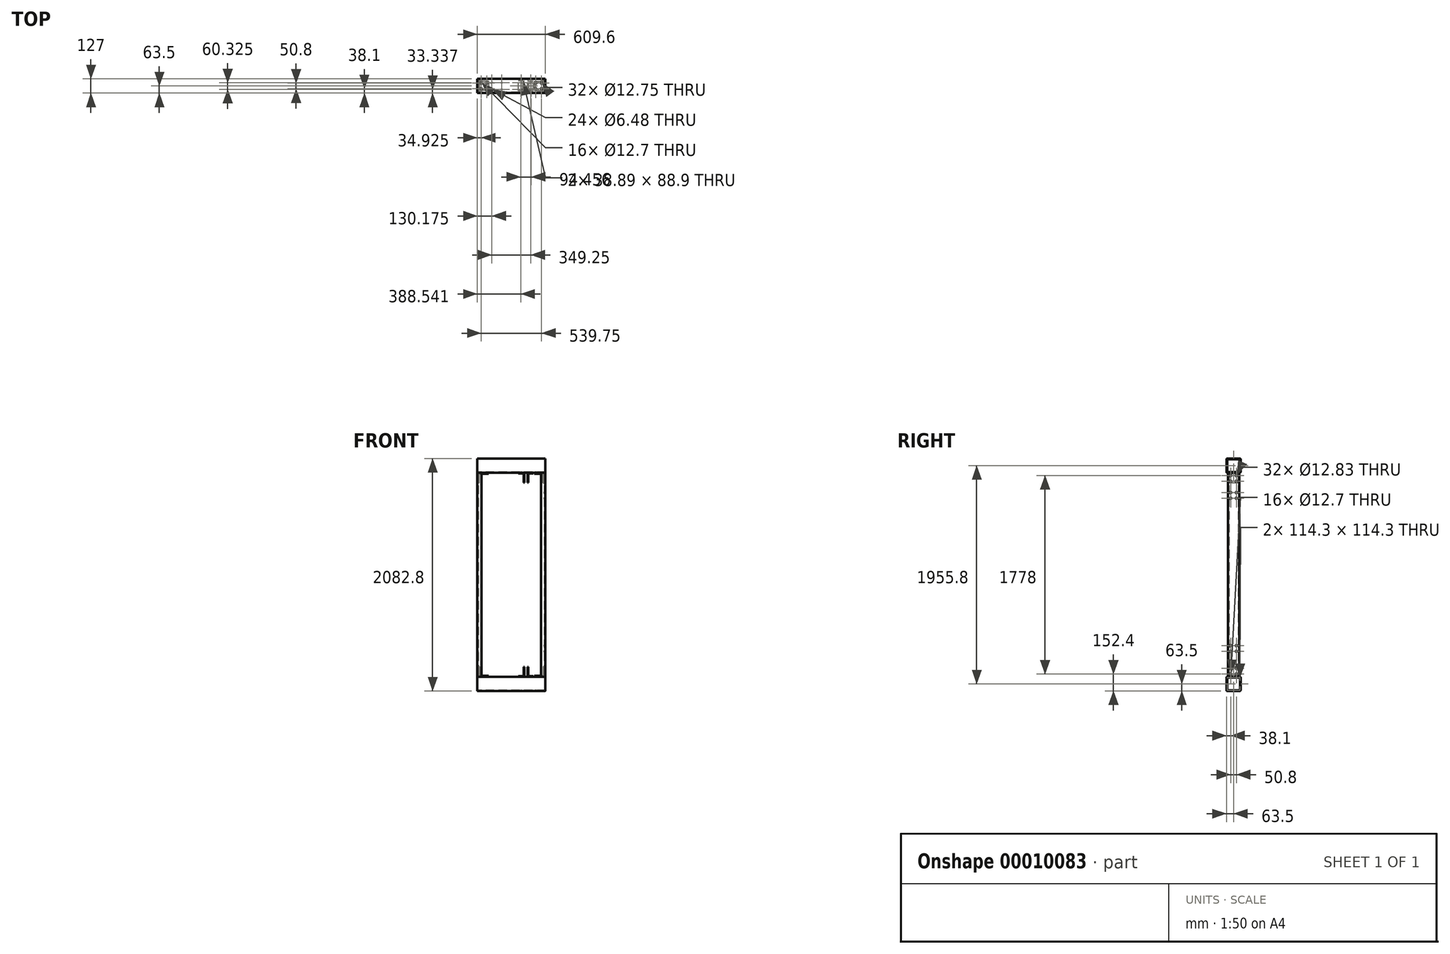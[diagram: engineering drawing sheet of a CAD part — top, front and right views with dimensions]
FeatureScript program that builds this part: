
annotation { "Feature Type Name" : "Feature", "Feature Type Description" : "" }
export const myFeature = defineFeature(function(context is Context, id is Id, definition is map)
    precondition{}
    {
        {
            var Q0;
            Q0=qCreatedBy(makeId("Front.planeOp"),FACE);
            cPlane(context, id + "F0", {"entities" : qUnion([Q0]), "cplaneType" : CPlaneType.OFFSET, "offset" : 41.27 * mm, "width" : 152.4 * mm, "height" : 152.4 * mm});
        }
        {
            var Q0;
            Q0=qCreatedBy(makeId("Top.planeOp"),FACE);
            cPlane(context, id + "F1", {"entities" : qUnion([Q0]), "cplaneType" : CPlaneType.OFFSET, "offset" : 977.9 * mm, "width" : 152.4 * mm, "height" : 152.4 * mm});
        }
        {
            var Q0;
            Q0=qCreatedBy(makeId("Right.planeOp"),FACE);
            var sketch = newSketch(context, id + "F2", { "sketchPlane" : qUnion([Q0])});
            skLineSegment(sketch, "E0.bottom", {"start": v(-57.15, 63.5) * mm, "end": v(57.15, 63.5) * mm});
            skLineSegment(sketch, "E0.top", {"start": v(-57.15, -63.5) * mm, "end": v(57.15, -63.5) * mm});
            skLineSegment(sketch, "E0.left", {"start": v(-63.5, 57.15) * mm, "end": v(-63.5, -57.15) * mm});
            skLineSegment(sketch, "E0.right", {"start": v(63.5, 57.15) * mm, "end": v(63.5, -57.15) * mm});
            skLineSegment(sketch, "E1.bottom", {"start": v(-57.15, 57.15) * mm, "end": v(57.15, 57.15) * mm});
            skLineSegment(sketch, "E1.top", {"start": v(-57.15, -57.15) * mm, "end": v(57.15, -57.15) * mm});
            skLineSegment(sketch, "E1.left", {"start": v(-57.15, 57.15) * mm, "end": v(-57.15, -57.15) * mm});
            skLineSegment(sketch, "E1.right", {"start": v(57.15, 57.15) * mm, "end": v(57.15, -57.15) * mm});
            skPoint(sketch, "E2.visualSharp", {"position": v(63.5, 63.5) * mm});
            skArc(sketch, "E2.filletArc", {"start": v(63.5, 57.15) * mm, "mid": v(61.64, 61.64) * mm, "end": v(57.15, 63.5) * mm});
            skPoint(sketch, "E3.visualSharp", {"position": v(63.5, -63.5) * mm});
            skArc(sketch, "E3.filletArc", {"start": v(57.15, -63.5) * mm, "mid": v(61.64, -61.64) * mm, "end": v(63.5, -57.15) * mm});
            skPoint(sketch, "E4.visualSharp", {"position": v(-63.5, -63.5) * mm});
            skArc(sketch, "E4.filletArc", {"start": v(-63.5, -57.15) * mm, "mid": v(-61.64, -61.64) * mm, "end": v(-57.15, -63.5) * mm});
            skPoint(sketch, "E5.visualSharp", {"position": v(-63.5, 63.5) * mm});
            skArc(sketch, "E5.filletArc", {"start": v(-57.15, 63.5) * mm, "mid": v(-61.64, 61.64) * mm, "end": v(-63.5, 57.15) * mm});
            skLineSegment(sketch, "E6", {"start": v(-57.15, 57.15) * mm, "end": v(57.15, -57.15) * mm});
            skSolve(sketch);
        }
        {
            var Q0;
            Q0 = qSketchRegion(id + "F2", true);
            extrude(context, id + "F3", {"entities" : qUnion([Q0]), "endBound" : BoundingType.SYMMETRIC, "depth" : 609.6 * mm});
        }
        {
            var Q0;
            Q0=makeQuery(id+"F3.opExtrude","SWEPT_FACE",FACE,{"disambiguationData":[OSD([sQuery(id+"F2.wireOp",EDGE,"E0.bottom")])]});
            var sketch = newSketch(context, id + "F4", { "sketchPlane" : qUnion([Q0])});
            skCircle(sketch, "E7", {"center": v(219.08, 25.4) * mm, "radius": 6.38 * mm});
            skCircle(sketch, "E8", {"center": v(219.08, -25.4) * mm, "radius": 6.38 * mm});
            skCircle(sketch, "E9", {"center": v(269.88, 25.4) * mm, "radius": 6.38 * mm});
            skCircle(sketch, "E10", {"center": v(269.88, -25.4) * mm, "radius": 6.38 * mm});
            skCircle(sketch, "E11", {"center": v(-219.08, 25.4) * mm, "radius": 6.38 * mm});
            skCircle(sketch, "E12", {"center": v(-269.88, 25.4) * mm, "radius": 6.38 * mm});
            skCircle(sketch, "E13", {"center": v(-219.08, -25.4) * mm, "radius": 6.38 * mm});
            skCircle(sketch, "E14", {"center": v(-269.88, -25.4) * mm, "radius": 6.38 * mm});
            skLineSegment(sketch, "E15", {"start": v(269.88, 25.4) * mm, "end": v(269.88, -25.4) * mm});
            skLineSegment(sketch, "E16", {"start": v(269.88, 0) * mm, "end": v(304.8, 0) * mm});
            skCircle(sketch, "E17", {"center": v(174.63, 30.16) * mm, "radius": 3.24 * mm});
            skCircle(sketch, "E18", {"center": v(174.63, -30.16) * mm, "radius": 3.24 * mm});
            skCircle(sketch, "E19", {"center": v(87.31, 30.16) * mm, "radius": 3.24 * mm});
            skCircle(sketch, "E20", {"center": v(87.31, -30.16) * mm, "radius": 3.24 * mm});
            skCircle(sketch, "E21", {"center": v(-174.63, 30.16) * mm, "radius": 3.24 * mm});
            skCircle(sketch, "E22", {"center": v(-87.31, 30.16) * mm, "radius": 3.24 * mm});
            skCircle(sketch, "E23", {"center": v(-174.63, -30.16) * mm, "radius": 3.24 * mm});
            skCircle(sketch, "E24", {"center": v(-87.31, -30.16) * mm, "radius": 3.24 * mm});
            skLineSegment(sketch, "E25", {"start": v(174.63, 30.16) * mm, "end": v(174.63, -30.16) * mm});
            skLineSegment(sketch, "E26", {"start": v(174.63, 0) * mm, "end": v(269.88, 0) * mm});
            skSolve(sketch);
        }
        {
            var Q0;
            Q0 = qSketchRegion(id + "F4", true);
            extrude(context, id + "F5", {"entities" : qUnion([Q0]), "operationType" : NewBodyOperationType.REMOVE, "endBound" : BoundingType.THROUGH_ALL, "oppositeDirection" : true, "depth" : 25.4 * mm});
        }
        {
            var Q0;
            Q0=qCreatedBy(id+"F0.planeOp",FACE);
            var sketch = newSketch(context, id + "F6", { "sketchPlane" : qUnion([Q0])});
            skLineSegment(sketch, "E27.bottom", {"start": v(204.47, 73.03) * mm, "end": v(279.4, 73.03) * mm});
            skLineSegment(sketch, "E27.top", {"start": v(204.47, 63.5) * mm, "end": v(279.4, 63.5) * mm});
            skLineSegment(sketch, "E27.left", {"start": v(204.47, 73.03) * mm, "end": v(204.47, 63.5) * mm});
            skLineSegment(sketch, "E28.bottom", {"start": v(285.75, 154.3) * mm, "end": v(295.28, 154.3) * mm});
            skLineSegment(sketch, "E28.left", {"start": v(285.75, 154.3) * mm, "end": v(285.75, 79.37) * mm});
            skLineSegment(sketch, "E28.right", {"start": v(295.28, 154.3) * mm, "end": v(295.28, 79.37) * mm});
            skLineSegment(sketch, "E29.bottom", {"start": v(-204.47, 73.03) * mm, "end": v(-279.4, 73.03) * mm});
            skLineSegment(sketch, "E29.top", {"start": v(-204.47, 63.5) * mm, "end": v(-279.4, 63.5) * mm});
            skLineSegment(sketch, "E29.left", {"start": v(-204.47, 73.03) * mm, "end": v(-204.47, 63.5) * mm});
            skLineSegment(sketch, "E30.bottom", {"start": v(-285.75, 154.3) * mm, "end": v(-295.28, 154.3) * mm});
            skLineSegment(sketch, "E30.left", {"start": v(-285.75, 154.3) * mm, "end": v(-285.75, 79.38) * mm});
            skLineSegment(sketch, "E30.right", {"start": v(-295.28, 154.3) * mm, "end": v(-295.28, 79.38) * mm});
            skArc(sketch, "E31", {"start": v(279.4, 73.02) * mm, "mid": v(283.9, 74.88) * mm, "end": v(285.75, 79.37) * mm});
            skArc(sketch, "E32", {"start": v(279.4, 63.5) * mm, "mid": v(290.63, 68.15) * mm, "end": v(295.28, 79.37) * mm});
            skArc(sketch, "E33", {"start": v(-295.28, 79.38) * mm, "mid": v(-290.63, 68.15) * mm, "end": v(-279.4, 63.5) * mm});
            skArc(sketch, "E34", {"start": v(-279.4, 73.03) * mm, "mid": v(-283.9, 74.88) * mm, "end": v(-285.75, 79.38) * mm});
            skSolve(sketch);
        }
        {
            var Q0;
            Q0=makeQuery(id+"F6.imprint","IMPRINT",FACE,{"disambiguationData":[TD([[makeQuery(id+"F6.imprint","IMPRINT",EDGE,{"derivedFrom":sQuery(id+"F6.wireOp",EDGE,"E27.bottom")}),-1.0]])]});
            extrude(context, id + "F7", {"entities" : qUnion([Q0]), "oppositeDirection" : true, "depth" : 82.55 * mm});
        }
        {
            var Q0;
            Q0=makeQuery(id+"F7.opExtrude","SWEPT_FACE",FACE,{"disambiguationData":[OSD([sQuery(id+"F6.wireOp",EDGE,"E28.left")])]});
            var sketch = newSketch(context, id + "F8", { "sketchPlane" : qUnion([Q0])});
            skCircle(sketch, "E35", {"center": v(-25.4, 139.7) * mm, "radius": 6.35 * mm});
            skCircle(sketch, "E36", {"center": v(25.4, 139.7) * mm, "radius": 6.35 * mm});
            skCircle(sketch, "E37", {"center": v(-25.4, 88.9) * mm, "radius": 6.35 * mm});
            skCircle(sketch, "E38", {"center": v(25.4, 88.9) * mm, "radius": 6.35 * mm});
            skLineSegment(sketch, "E39", {"start": v(-25.4, 139.7) * mm, "end": v(25.4, 139.7) * mm});
            skLineSegment(sketch, "E40", {"start": v(0, 139.7) * mm, "end": v(0, 154.3) * mm});
            skSolve(sketch);
        }
        {
            var Q0;
            Q0 = qSketchRegion(id + "F8", true);
            extrude(context, id + "F9", {"entities" : qUnion([Q0]), "operationType" : NewBodyOperationType.REMOVE, "oppositeDirection" : true, "depth" : 9.52 * mm});
        }
        {
            var Q0;
            Q0=makeQuery(id+"F7.opExtrude","SWEPT_FACE",FACE,{"disambiguationData":[OSD([sQuery(id+"F6.wireOp",EDGE,"E27.bottom")])]});
            var sketch = newSketch(context, id + "F10", { "sketchPlane" : qUnion([Q0])});
            skCircle(sketch, "E41", {"center": v(269.88, 25.4) * mm, "radius": 6.35 * mm});
            skCircle(sketch, "E42", {"center": v(219.08, 25.4) * mm, "radius": 6.35 * mm});
            skCircle(sketch, "E43", {"center": v(219.08, -25.4) * mm, "radius": 6.35 * mm});
            skCircle(sketch, "E44", {"center": v(269.88, -25.4) * mm, "radius": 6.35 * mm});
            skLineSegment(sketch, "E45", {"start": v(269.88, 25.4) * mm, "end": v(269.88, -25.4) * mm});
            skLineSegment(sketch, "E46", {"start": v(269.88, 0) * mm, "end": v(279.4, 0) * mm});
            skSolve(sketch);
        }
        {
            var Q0;
            Q0 = qSketchRegion(id + "F10", true);
            extrude(context, id + "F11", {"entities" : qUnion([Q0]), "operationType" : NewBodyOperationType.REMOVE, "oppositeDirection" : true, "depth" : 9.52 * mm});
        }
        {
            var Q0;
            Q0=makeQuery(id+"F3.opExtrude","SWEPT_FACE",FACE,{"disambiguationData":[OSD([sQuery(id+"F2.wireOp",EDGE,"E0.bottom")])]});
            var sketch = newSketch(context, id + "F12", { "sketchPlane" : qUnion([Q0])});
            skLineSegment(sketch, "E47.bottom", {"start": v(266.7, 50.8) * mm, "end": v(304.8, 50.8) * mm});
            skLineSegment(sketch, "E47.top", {"start": v(266.7, -50.8) * mm, "end": v(304.8, -50.8) * mm});
            skLineSegment(sketch, "E47.left", {"start": v(266.7, 50.8) * mm, "end": v(266.7, 44.45) * mm});
            skLineSegment(sketch, "E47.right", {"start": v(304.8, 50.8) * mm, "end": v(304.8, -50.8) * mm});
            skLineSegment(sketch, "E48", {"start": v(266.7, 44.45) * mm, "end": v(295.27, 41.28) * mm});
            skLineSegment(sketch, "E49", {"start": v(295.28, 41.28) * mm, "end": v(295.28, -41.27) * mm});
            skLineSegment(sketch, "E50", {"start": v(295.28, -41.27) * mm, "end": v(266.7, -44.45) * mm});
            skLineSegment(sketch, "E51.trimOffspring", {"start": v(266.7, -44.45) * mm, "end": v(266.7, -50.8) * mm});
            skLineSegment(sketch, "E52", {"start": v(295.28, 0) * mm, "end": v(197.91, 0) * mm});
            skSolve(sketch);
        }
        {
            var Q0;
            Q0 = qSketchRegion(id + "F12", true);
            extrude(context, id + "F13", {"entities" : qUnion([Q0]), "depth" : 1828.8 * mm});
        }
        {
            var Q0;
            Q0=makeQuery(id+"F13.opExtrude","SWEPT_FACE",FACE,{"disambiguationData":[OSD([sQuery(id+"F12.wireOp",EDGE,"E47.right")])]});
            var sketch = newSketch(context, id + "F14", { "sketchPlane" : qUnion([Q0])});
            skCircle(sketch, "E53", {"center": v(25.4, 88.9) * mm, "radius": 6.41 * mm});
            skCircle(sketch, "E54", {"center": v(-25.4, 88.9) * mm, "radius": 6.41 * mm});
            skCircle(sketch, "E55", {"center": v(25.4, 139.7) * mm, "radius": 6.41 * mm});
            skCircle(sketch, "E56", {"center": v(-25.4, 139.7) * mm, "radius": 6.41 * mm});
            skCircle(sketch, "E57", {"center": v(25.4, 292.1) * mm, "radius": 6.41 * mm});
            skCircle(sketch, "E58", {"center": v(-25.4, 292.1) * mm, "radius": 6.41 * mm});
            skCircle(sketch, "E59", {"center": v(25.4, 342.9) * mm, "radius": 6.41 * mm});
            skCircle(sketch, "E60", {"center": v(-25.4, 342.9) * mm, "radius": 6.41 * mm});
            skCircle(sketch, "E61", {"center": v(25.4, 1663.7) * mm, "radius": 6.41 * mm});
            skCircle(sketch, "E62", {"center": v(-25.4, 1663.7) * mm, "radius": 6.41 * mm});
            skCircle(sketch, "E63", {"center": v(25.4, 1714.5) * mm, "radius": 6.41 * mm});
            skCircle(sketch, "E64", {"center": v(-25.4, 1714.5) * mm, "radius": 6.41 * mm});
            skCircle(sketch, "E65", {"center": v(25.4, 1816.1) * mm, "radius": 6.41 * mm});
            skCircle(sketch, "E66", {"center": v(-25.4, 1816.1) * mm, "radius": 6.41 * mm});
            skCircle(sketch, "E67", {"center": v(25.4, 1866.9) * mm, "radius": 6.41 * mm});
            skCircle(sketch, "E68", {"center": v(-25.4, 1866.9) * mm, "radius": 6.41 * mm});
            skLineSegment(sketch, "E69", {"start": v(-25.4, 88.9) * mm, "end": v(25.4, 88.9) * mm});
            skLineSegment(sketch, "E70", {"start": v(0, 88.9) * mm, "end": v(0, 63.5) * mm});
            skSolve(sketch);
        }
        {
            var Q0;
            Q0 = qSketchRegion(id + "F14", true);
            extrude(context, id + "F15", {"entities" : qUnion([Q0]), "operationType" : NewBodyOperationType.REMOVE, "oppositeDirection" : true, "depth" : 9.52 * mm});
        }
        {
            var Q0;
            Q0=makeQuery(id+"F3.opExtrude","SWEPT_FACE",FACE,{"disambiguationData":[OSD([sQuery(id+"F2.wireOp",EDGE,"E0.bottom")])]});
            var sketch = newSketch(context, id + "F16", { "sketchPlane" : qUnion([Q0])});
            skLineSegment(sketch, "E71", {"start": v(87.31, -30.16) * mm, "end": v(174.63, -30.16) * mm});
            skSolve(sketch);
        }
        {
            var Q0;
            Q0=qCreatedBy(makeId("Front.planeOp"),FACE);
            var sketch = newSketch(context, id + "F17", { "sketchPlane" : qUnion([Q0])});
            skLineSegment(sketch, "E72", {"start": v(64.3, 63.5) * mm, "end": v(64.3, 69.85) * mm});
            skLineSegment(sketch, "E73", {"start": v(64.3, 69.85) * mm, "end": v(103.19, 69.85) * mm});
            skLineSegment(sketch, "E74", {"start": v(109.54, 76.2) * mm, "end": v(109.54, 152.4) * mm});
            skLineSegment(sketch, "E75", {"start": v(109.54, 152.4) * mm, "end": v(115.89, 152.4) * mm});
            skLineSegment(sketch, "E76", {"start": v(115.89, 152.4) * mm, "end": v(115.89, 76.2) * mm});
            skLineSegment(sketch, "E77", {"start": v(103.19, 63.5) * mm, "end": v(64.3, 63.5) * mm});
            skLineSegment(sketch, "E78", {"start": v(130.97, 152.4) * mm, "end": v(130.97, 63.5) * mm});
            skPoint(sketch, "E79.end.orphan", {"position": v(191.19, 152.4) * mm});
            skPoint(sketch, "E80.visualSharp", {"position": v(109.54, 69.85) * mm});
            skArc(sketch, "E80.filletArc", {"start": v(103.19, 69.85) * mm, "mid": v(107.68, 71.7) * mm, "end": v(109.54, 76.2) * mm});
            skPoint(sketch, "E81.visualSharp", {"position": v(115.89, 63.5) * mm});
            skArc(sketch, "E81.filletArc", {"start": v(103.19, 63.5) * mm, "mid": v(112.17, 67.22) * mm, "end": v(115.89, 76.2) * mm});
            skLineSegment(sketch, "E82", {"start": v(87.31, 69.85) * mm, "end": v(87.31, 83.64) * mm});
            skLineSegment(sketch, "E83.MirrorCS", {"start": v(197.64, 63.5) * mm, "end": v(197.64, 69.85) * mm});
            skLineSegment(sketch, "E84.MirrorCS", {"start": v(197.64, 69.85) * mm, "end": v(158.75, 69.85) * mm});
            skLineSegment(sketch, "E85.MirrorCS", {"start": v(174.63, 69.85) * mm, "end": v(174.63, 83.64) * mm});
            skLineSegment(sketch, "E86.MirrorCS", {"start": v(146.05, 152.4) * mm, "end": v(146.05, 76.2) * mm});
            skLineSegment(sketch, "E87.MirrorCS", {"start": v(152.4, 76.2) * mm, "end": v(152.4, 152.4) * mm});
            skLineSegment(sketch, "E88.MirrorCS", {"start": v(152.4, 152.4) * mm, "end": v(146.05, 152.4) * mm});
            skLineSegment(sketch, "E89.MirrorCS", {"start": v(158.75, 63.5) * mm, "end": v(197.64, 63.5) * mm});
            skArc(sketch, "E90.MirrorCS", {"start": v(158.75, 69.85) * mm, "mid": v(154.26, 71.7) * mm, "end": v(152.4, 76.2) * mm});
            skArc(sketch, "E91.MirrorCS", {"start": v(158.75, 63.5) * mm, "mid": v(149.77, 67.22) * mm, "end": v(146.05, 76.2) * mm});
            skLineSegment(sketch, "E92", {"start": v(87.31, 63.5) * mm, "end": v(174.63, 63.5) * mm});
            skSolve(sketch);
        }
        {
            var Q0;
            {var subQ6=sQuery(id+"F17.wireOp",EDGE,"E83.MirrorCS");Q0=makeQuery(id+"F17.imprint","IMPRINT",FACE,{"disambiguationData":[TD([[makeQuery(id+"F17.imprint","IMPRINT",EDGE,{"derivedFrom":subQ6}),1.0]])]});}
            var Q1;
            {var subQ6=sQuery(id+"F17.wireOp",EDGE,"E72");Q1=makeQuery(id+"F17.imprint","IMPRINT",FACE,{"disambiguationData":[TD([[makeQuery(id+"F17.imprint","IMPRINT",EDGE,{"derivedFrom":subQ6}),-1.0]])]});}
            extrude(context, id + "F18", {"entities" : qUnion([Q0, Q1]), "operationType" : NewBodyOperationType.ADD, "endBound" : BoundingType.SYMMETRIC, "depth" : 88.9 * mm});
        }
        {
            var Q0;
            Q0=makeQuery(id+"F7.opExtrude","SWEPT_BODY",BODY,{"disambiguationData":[OSD([sQuery(id+"F6.wireOp",EDGE,"E27.bottom"),sQuery(id+"F6.wireOp",EDGE,"E27.top"),sQuery(id+"F6.wireOp",EDGE,"E27.left"),sQuery(id+"F6.wireOp",EDGE,"E28.bottom"),sQuery(id+"F6.wireOp",EDGE,"E28.left"),sQuery(id+"F6.wireOp",EDGE,"E28.right"),sQuery(id+"F6.wireOp",EDGE,"E31"),sQuery(id+"F6.wireOp",EDGE,"E32")])]});
            var Q1;
            Q1=makeQuery(id+"F13.opExtrude","SWEPT_BODY",BODY,{"disambiguationData":[OSD([sQuery(id+"F12.wireOp",EDGE,"E47.bottom"),sQuery(id+"F12.wireOp",EDGE,"E47.top"),sQuery(id+"F12.wireOp",EDGE,"E47.left"),sQuery(id+"F12.wireOp",EDGE,"E47.right"),sQuery(id+"F12.wireOp",EDGE,"E48"),sQuery(id+"F12.wireOp",EDGE,"E49"),sQuery(id+"F12.wireOp",EDGE,"E50"),sQuery(id+"F12.wireOp",EDGE,"E51.trimOffspring")])]});
            var Q2;
            Q2=qCreatedBy(makeId("Right.planeOp"),FACE);
            mirror(context, id + "F19", {"entities" : qUnion([Q0, Q1]), "mirrorPlane" : qUnion([Q2])});
        }
        {
            var Q0;
            Q0=makeQuery(id+"F3.opExtrude","SWEPT_BODY",BODY,{"disambiguationData":[OSD([sQuery(id+"F2.wireOp",EDGE,"E0.bottom"),sQuery(id+"F2.wireOp",EDGE,"E0.top"),sQuery(id+"F2.wireOp",EDGE,"E0.left"),sQuery(id+"F2.wireOp",EDGE,"E0.right"),sQuery(id+"F2.wireOp",EDGE,"E1.bottom"),sQuery(id+"F2.wireOp",EDGE,"E1.top"),sQuery(id+"F2.wireOp",EDGE,"E1.left"),sQuery(id+"F2.wireOp",EDGE,"E1.right"),sQuery(id+"F2.wireOp",EDGE,"E2.filletArc"),sQuery(id+"F2.wireOp",EDGE,"E3.filletArc"),sQuery(id+"F2.wireOp",EDGE,"E4.filletArc"),sQuery(id+"F2.wireOp",EDGE,"E5.filletArc")])]});
            var Q1;
            Q1=makeQuery(id+"F7.opExtrude","SWEPT_BODY",BODY,{"disambiguationData":[OSD([sQuery(id+"F6.wireOp",EDGE,"E27.bottom"),sQuery(id+"F6.wireOp",EDGE,"E27.top"),sQuery(id+"F6.wireOp",EDGE,"E27.left"),sQuery(id+"F6.wireOp",EDGE,"E28.bottom"),sQuery(id+"F6.wireOp",EDGE,"E28.left"),sQuery(id+"F6.wireOp",EDGE,"E28.right"),sQuery(id+"F6.wireOp",EDGE,"E31"),sQuery(id+"F6.wireOp",EDGE,"E32")])]});
            var Q2;
            Q2=makeQuery(id+"F19.opPattern","COPY",BODY,{"derivedFrom":makeQuery(id+"F7.opExtrude","SWEPT_BODY",BODY,{"disambiguationData":[OSD([sQuery(id+"F6.wireOp",EDGE,"E27.bottom"),sQuery(id+"F6.wireOp",EDGE,"E27.top"),sQuery(id+"F6.wireOp",EDGE,"E27.left"),sQuery(id+"F6.wireOp",EDGE,"E28.bottom"),sQuery(id+"F6.wireOp",EDGE,"E28.left"),sQuery(id+"F6.wireOp",EDGE,"E28.right"),sQuery(id+"F6.wireOp",EDGE,"E31"),sQuery(id+"F6.wireOp",EDGE,"E32")])]}),"instanceName":"1"});
            var Q3;
            Q3=qCreatedBy(id+"F1.planeOp",FACE);
            mirror(context, id + "F20", {"entities" : qUnion([Q0, Q1, Q2]), "mirrorPlane" : qUnion([Q3])});
        }
    });
